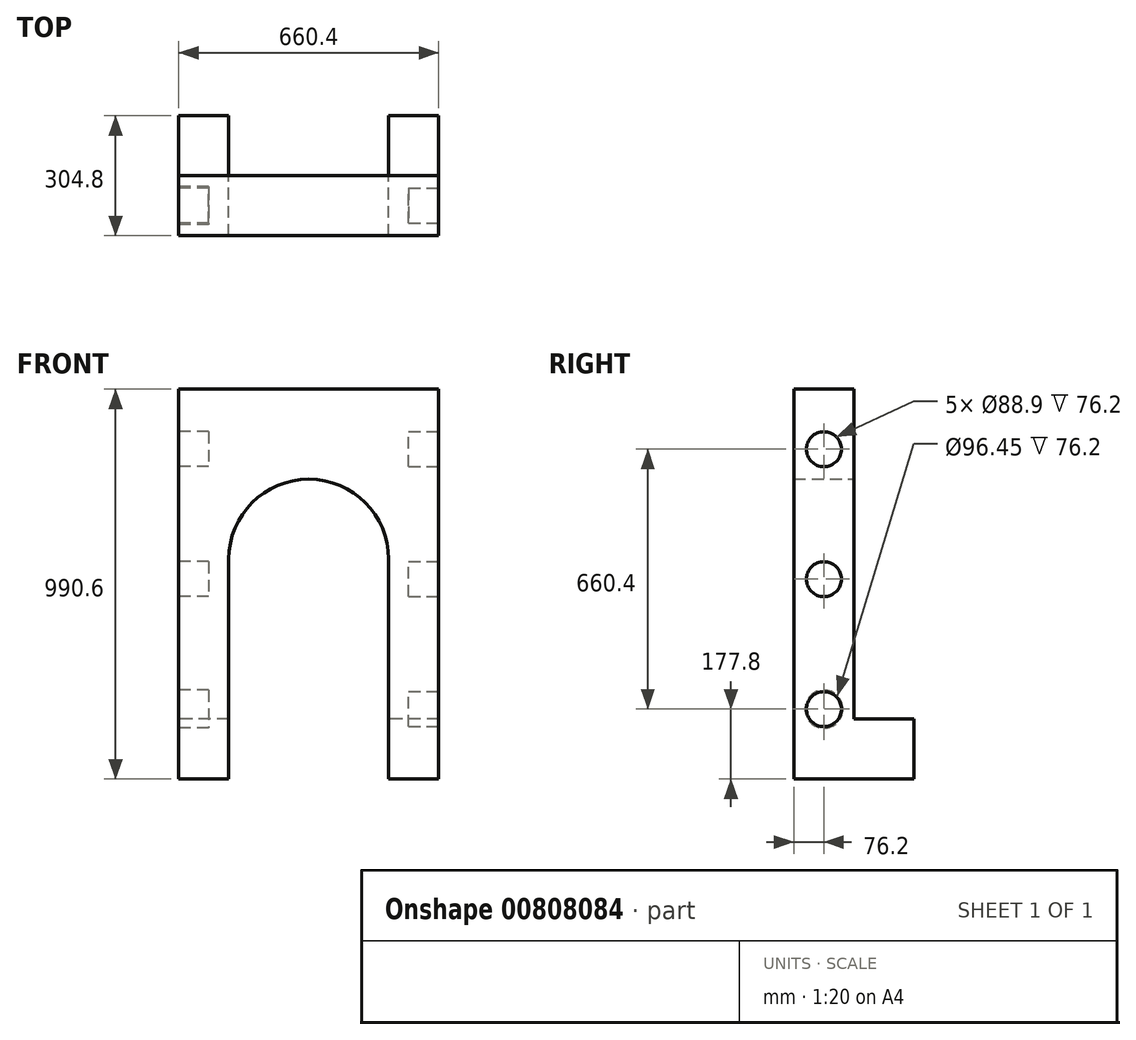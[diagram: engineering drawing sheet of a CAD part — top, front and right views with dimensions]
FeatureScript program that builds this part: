
annotation { "Feature Type Name" : "Feature", "Feature Type Description" : "" }
export const myFeature = defineFeature(function(context is Context, id is Id, definition is map)
    precondition{}
    {
        {
            var Q0;
            Q0=qCreatedBy(makeId("Front.planeOp"),FACE);
            var sketch = newSketch(context, id + "F0", { "sketchPlane" : qUnion([Q0])});
            skLineSegment(sketch, "E0.bottom", {"start": v(-330.2, -495.3) * mm, "end": v(330.2, -495.3) * mm});
            skLineSegment(sketch, "E0.top", {"start": v(-330.2, 495.3) * mm, "end": v(330.2, 495.3) * mm});
            skLineSegment(sketch, "E0.left", {"start": v(-330.2, -495.3) * mm, "end": v(-330.2, 495.3) * mm});
            skLineSegment(sketch, "E0.right", {"start": v(330.2, -495.3) * mm, "end": v(330.2, 495.3) * mm});
            skPoint(sketch, "E0.middle", {"position": v(0, 0) * mm});
            skArc(sketch, "E1", {"start": v(203.2, 63.5) * mm, "mid": v(0, 266.7) * mm, "end": v(-203.2, 63.5) * mm});
            skLineSegment(sketch, "E2", {"start": v(203.2, 63.5) * mm, "end": v(203.2, -495.3) * mm});
            skLineSegment(sketch, "E3", {"start": v(-203.2, 63.5) * mm, "end": v(-203.2, -495.3) * mm});
            skPoint(sketch, "E4.start.orphan", {"position": v(0, -495.3) * mm});
            skSolve(sketch);
        }
        {
            var Q0;
            Q0=makeQuery(id+"F0.imprint","IMPRINT",FACE,{"disambiguationData":[TD([[makeQuery(id+"F0.imprint","IMPRINT",EDGE,{"derivedFrom":sQuery(id+"F0.wireOp",EDGE,"E0.top")}),-1.0]])]});
            extrude(context, id + "F1", {"entities" : qUnion([Q0]), "depth" : 152.4 * mm, "offsetDistance" : 25.4 * mm});
        }
        {
            var Q0;
            Q0=makeQuery(id+"F1.opExtrude","CAP_FACE",FACE,{"disambiguationData":[OSD([sQuery(id+"F0.wireOp",EDGE,"E0.bottom"),sQuery(id+"F0.wireOp",EDGE,"E0.top"),sQuery(id+"F0.wireOp",EDGE,"E0.left"),sQuery(id+"F0.wireOp",EDGE,"E0.right"),sQuery(id+"F0.wireOp",EDGE,"E1"),sQuery(id+"F0.wireOp",EDGE,"E2"),sQuery(id+"F0.wireOp",EDGE,"E3")])],"isStart":true});
            var sketch = newSketch(context, id + "F2", { "sketchPlane" : qUnion([Q0])});
            skLineSegment(sketch, "E5.bottom", {"start": v(-330.2, -495.3) * mm, "end": v(-203.2, -495.3) * mm});
            skLineSegment(sketch, "E5.top", {"start": v(-330.2, -342.9) * mm, "end": v(-203.2, -342.9) * mm});
            skLineSegment(sketch, "E5.left", {"start": v(-330.2, -495.3) * mm, "end": v(-330.2, -342.9) * mm});
            skLineSegment(sketch, "E5.right", {"start": v(-203.2, -495.3) * mm, "end": v(-203.2, -342.9) * mm});
            skLineSegment(sketch, "E6.bottom", {"start": v(203.2, -495.3) * mm, "end": v(330.2, -495.3) * mm});
            skLineSegment(sketch, "E6.top", {"start": v(203.2, -342.9) * mm, "end": v(330.2, -342.9) * mm});
            skLineSegment(sketch, "E6.left", {"start": v(203.2, -495.3) * mm, "end": v(203.2, -342.9) * mm});
            skLineSegment(sketch, "E6.right", {"start": v(330.2, -495.3) * mm, "end": v(330.2, -342.9) * mm});
            skSolve(sketch);
        }
        {
            var Q0;
            Q0 = qSketchRegion(id + "F2", true);
            extrude(context, id + "F3", {"entities" : qUnion([Q0]), "operationType" : NewBodyOperationType.ADD, "depth" : 152.4 * mm, "offsetDistance" : 25.4 * mm});
        }
        {
            var Q0;
            Q0=makeQuery(id+"F3.boolean.opBoolean","MERGE",FACE,{"derivedFrom":[makeQuery(id+"F1.opExtrude","SWEPT_FACE",FACE,{"disambiguationData":[OSD([sQuery(id+"F0.wireOp",EDGE,"E0.left")])]}),makeQuery(id+"F3.opExtrude","SWEPT_FACE",FACE,{"disambiguationData":[OSD([sQuery(id+"F2.wireOp",EDGE,"E6.right")])]})]});
            var sketch = newSketch(context, id + "F4", { "sketchPlane" : qUnion([Q0])});
            skLineSegment(sketch, "E7.bottom", {"start": v(152.4, 495.3) * mm, "end": v(76.2, 495.3) * mm});
            skLineSegment(sketch, "E7.top", {"start": v(152.4, 342.9) * mm, "end": v(76.2, 342.9) * mm});
            skLineSegment(sketch, "E7.left", {"start": v(152.4, 495.3) * mm, "end": v(152.4, 342.9) * mm});
            skCircle(sketch, "E8", {"center": v(76.2, 342.9) * mm, "radius": 44.45 * mm});
            skLineSegment(sketch, "E9", {"start": v(76.2, 342.9) * mm, "end": v(76.2, 12.7) * mm});
            skCircle(sketch, "E10", {"center": v(76.2, 12.7) * mm, "radius": 44.45 * mm});
            skLineSegment(sketch, "E11", {"start": v(76.2, 12.7) * mm, "end": v(76.2, -317.5) * mm});
            skCircle(sketch, "E12", {"center": v(76.2, -317.5) * mm, "radius": 48.23 * mm});
            skSolve(sketch);
        }
        {
            var Q0;
            Q0 = qSketchRegion(id + "F4", true);
            extrude(context, id + "F5", {"entities" : qUnion([Q0]), "operationType" : NewBodyOperationType.REMOVE, "oppositeDirection" : true, "depth" : 76.2 * mm, "offsetDistance" : 25.4 * mm});
        }
        {
            var Q0;
            Q0=makeQuery(id+"F3.boolean.opBoolean","MERGE",FACE,{"derivedFrom":[makeQuery(id+"F1.opExtrude","SWEPT_FACE",FACE,{"disambiguationData":[OSD([sQuery(id+"F0.wireOp",EDGE,"E0.right")])]}),makeQuery(id+"F3.opExtrude","SWEPT_FACE",FACE,{"disambiguationData":[OSD([sQuery(id+"F2.wireOp",EDGE,"E5.left")])]})]});
            var sketch = newSketch(context, id + "F6", { "sketchPlane" : qUnion([Q0])});
            skLineSegment(sketch, "E13", {"start": v(0, 495.3) * mm, "end": v(0, 342.9) * mm});
            skCircle(sketch, "E14", {"center": v(-76.2, 342.9) * mm, "radius": 44.45 * mm});
            skPoint(sketch, "E15.trimOffspring.end.orphan", {"position": v(-152.4, 342.9) * mm});
            skPoint(sketch, "E16.start.orphan", {"position": v(-76.2, 495.3) * mm});
            skLineSegment(sketch, "E17", {"start": v(-76.2, 342.9) * mm, "end": v(-76.2, 12.7) * mm});
            skCircle(sketch, "E18", {"center": v(-76.2, 12.7) * mm, "radius": 44.45 * mm});
            skLineSegment(sketch, "E19", {"start": v(-76.2, 12.7) * mm, "end": v(-76.2, -317.5) * mm});
            skCircle(sketch, "E20", {"center": v(-76.2, -317.5) * mm, "radius": 44.45 * mm});
            skSolve(sketch);
        }
        {
            var Q0;
            Q0 = qSketchRegion(id + "F6", true);
            extrude(context, id + "F7", {"entities" : qUnion([Q0]), "operationType" : NewBodyOperationType.REMOVE, "oppositeDirection" : true, "depth" : 76.2 * mm, "offsetDistance" : 25.4 * mm});
        }
    });
